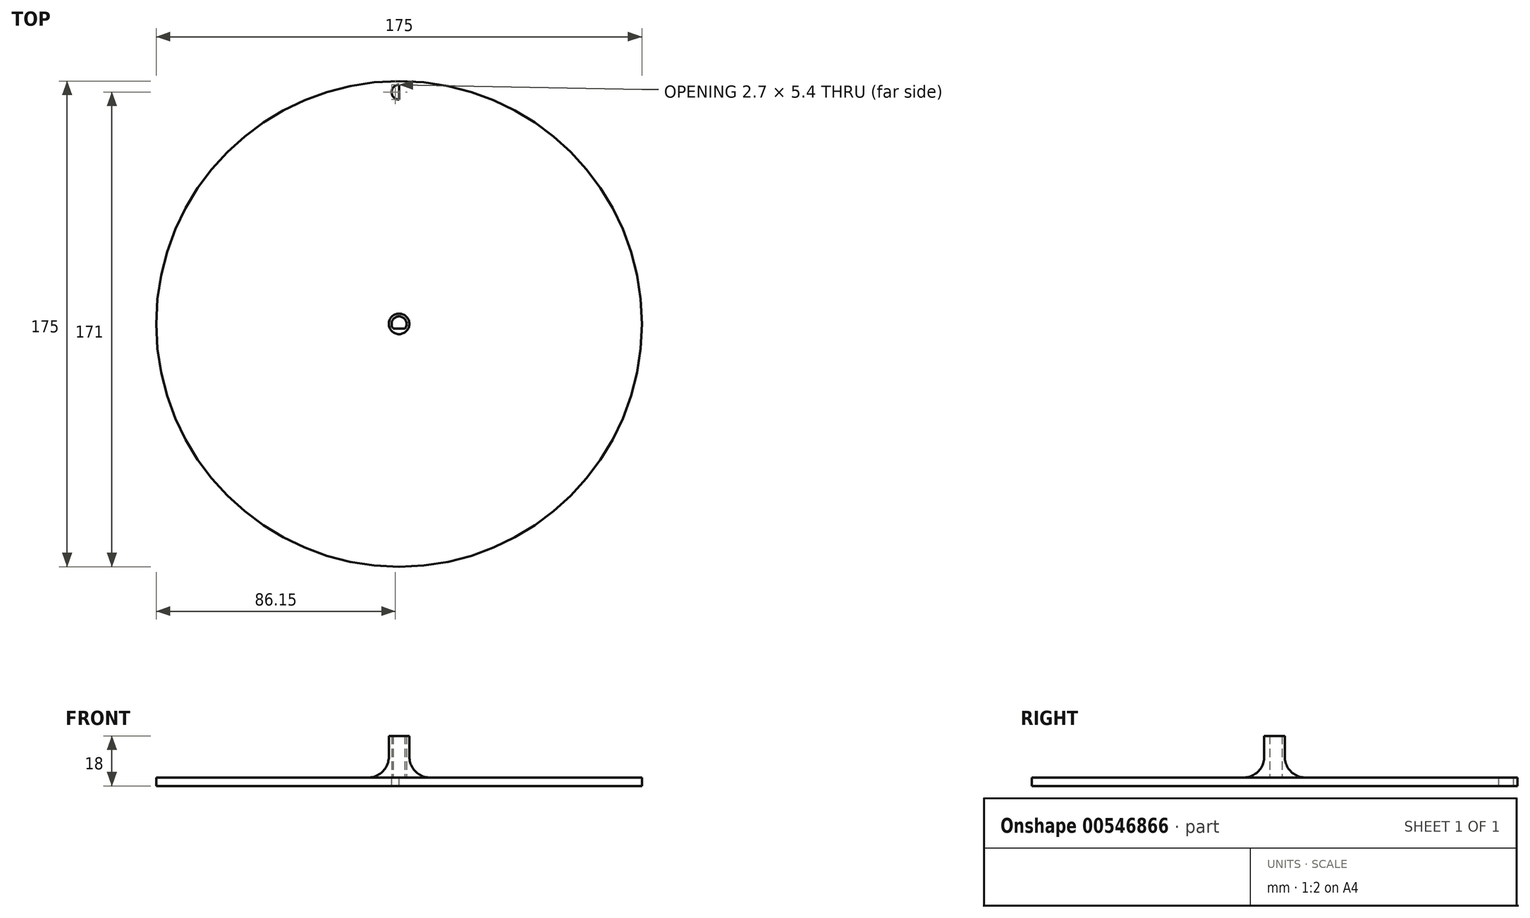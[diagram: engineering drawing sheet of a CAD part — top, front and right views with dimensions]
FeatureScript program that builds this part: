
annotation { "Feature Type Name" : "Feature", "Feature Type Description" : "" }
export const myFeature = defineFeature(function(context is Context, id is Id, definition is map)
    precondition{}
    {
        {
            var Q0;
            Q0=qCreatedBy(makeId("Top.planeOp"),FACE);
            var sketch = newSketch(context, id + "F0", { "sketchPlane" : qUnion([Q0])});
            skCircle(sketch, "E0", {"center": v(0, 0) * mm, "radius": 2.7 * mm});
            skLineSegment(sketch, "E1", {"start": v(0, 0) * mm, "end": v(0, -1.7) * mm});
            skLineSegment(sketch, "E2", {"start": v(0, -1.7) * mm, "end": v(2.1, -1.7) * mm});
            skLineSegment(sketch, "E3", {"start": v(0, -1.7) * mm, "end": v(-2.1, -1.7) * mm});
            skCircle(sketch, "E4", {"center": v(0, 0) * mm, "radius": 3.7 * mm});
            skCircle(sketch, "E5", {"center": v(0, 0) * mm, "radius": 7.4 * mm});
            skSolve(sketch);
        }
        {
            var Q0;
            {var subQ0=sQuery(id+"F0.wireOp",EDGE,"E2");Q0=makeQuery(id+"F0.imprint","IMPRINT",FACE,{"disambiguationData":[TD([[makeQuery(id+"F0.imprint","IMPRINT",EDGE,{"derivedFrom":subQ0}),-1.0]])]});}
            var Q1;
            Q1=makeQuery(id+"F0.imprint","IMPRINT",FACE,{"disambiguationData":[TD([[makeQuery(id+"F0.imprint","IMPRINT",EDGE,{"derivedFrom":sQuery(id+"F0.wireOp",EDGE,"E4")}),1.0]])]});
            extrude(context, id + "F1", {"entities" : qUnion([Q0, Q1]), "depth" : 15 * mm, "offsetDistance" : 25 * mm});
        }
        {
            var Q0;
            Q0=qCreatedBy(makeId("Top.planeOp"),FACE);
            var sketch = newSketch(context, id + "F2", { "sketchPlane" : qUnion([Q0])});
            skCircle(sketch, "E6", {"center": v(0, 0) * mm, "radius": 87.5 * mm});
            skLineSegment(sketch, "E7", {"start": v(0, 0) * mm, "end": v(0, 87.5) * mm});
            skLineSegment(sketch, "E8", {"start": v(0, 87.5) * mm, "end": v(0, 83.5) * mm});
            skCircle(sketch, "E9", {"center": v(0, 83.5) * mm, "radius": 2.7 * mm});
            skLineSegment(sketch, "E10", {"start": v(0, 83.5) * mm, "end": v(0, 81.8) * mm});
            skLineSegment(sketch, "E11", {"start": v(0, 81.8) * mm, "end": v(-2.1, 81.8) * mm});
            skLineSegment(sketch, "E12", {"start": v(-2.1, 81.8) * mm, "end": v(2.1, 81.8) * mm});
            skSolve(sketch);
        }
        {
            var Q0;
            Q0=qSketchRegion(id+"F2",true);
            var Q1;
            {var subQ0=sQuery(id+"F2.wireOp",EDGE,"E12");var subQ3=sQuery(id+"F2.wireOp",EDGE,"E9");var subQ5=makeQuery(id+"F2.imprint","INTERSECT",VERTEX,{"disambiguationData":[OD(0.0)],"derivedFrom":[subQ3,subQ0]});Q1=makeQuery(id+"F2.imprint","IMPRINT",FACE,{"disambiguationData":[TD([[makeQuery(id+"F2.imprint","IMPRINT",EDGE,{"disambiguationData":[TD([[subQ5,-1.0]])],"derivedFrom":subQ3}),1.0]])]});}
            var Q2;
            {var subQ0=sQuery(id+"F2.wireOp",EDGE,"E12");var subQ3=sQuery(id+"F2.wireOp",EDGE,"E9");var subQ5=makeQuery(id+"F2.imprint","INTERSECT",VERTEX,{"disambiguationData":[OD(1.0)],"derivedFrom":[subQ3,subQ0]});Q2=makeQuery(id+"F2.imprint","IMPRINT",FACE,{"disambiguationData":[TD([[makeQuery(id+"F2.imprint","IMPRINT",EDGE,{"disambiguationData":[TD([[subQ5,1.0]])],"derivedFrom":subQ3}),1.0]])]});}
            extrude(context, id + "F3", {"entities" : qUnion([Q0, Q1, Q2]), "operationType" : NewBodyOperationType.ADD, "oppositeDirection" : true, "depth" : 3 * mm, "offsetDistance" : 25 * mm});
        }
        {
            var Q0;
            Q0=qCreatedBy(makeId("Right.planeOp"),FACE);
            var sketch = newSketch(context, id + "F4", { "sketchPlane" : qUnion([Q0])});
            skLineSegment(sketch, "E13", {"start": v(0, 0) * mm, "end": v(0, 7.5) * mm});
            skLineSegment(sketch, "E14", {"start": v(0, 7.5) * mm, "end": v(3.7, 7.5) * mm});
            skLineSegment(sketch, "E15", {"start": v(0, 0) * mm, "end": v(11.2, 0) * mm});
            skLineSegment(sketch, "E16", {"start": v(3.7, 7.5) * mm, "end": v(3.7, 15) * mm});
            skArc(sketch, "E17", {"start": v(3.7, 7.5) * mm, "mid": v(5.9, 2.2) * mm, "end": v(11.2, 0) * mm});
            skLineSegment(sketch, "E18", {"start": v(3.7, 7.5) * mm, "end": v(3.7, 0) * mm});
            skSolve(sketch);
        }
        {
            var Q0;
            {var subQ0=sQuery(id+"F4.wireOp",EDGE,"E17");Q0=makeQuery(id+"F4.imprint","IMPRINT",FACE,{"disambiguationData":[TD([[makeQuery(id+"F4.imprint","IMPRINT",EDGE,{"derivedFrom":subQ0}),-1.0]])]});}
            var Q1;
            Q1=sQuery(id+"F4.wireOp",EDGE,"E13");
            revolve(context, id + "F5", {"operationType" : NewBodyOperationType.ADD, "entities" : qUnion([Q0]), "axis" : qUnion([Q1]), "revolveType" : RevolveType.FULL});
        }
    });
